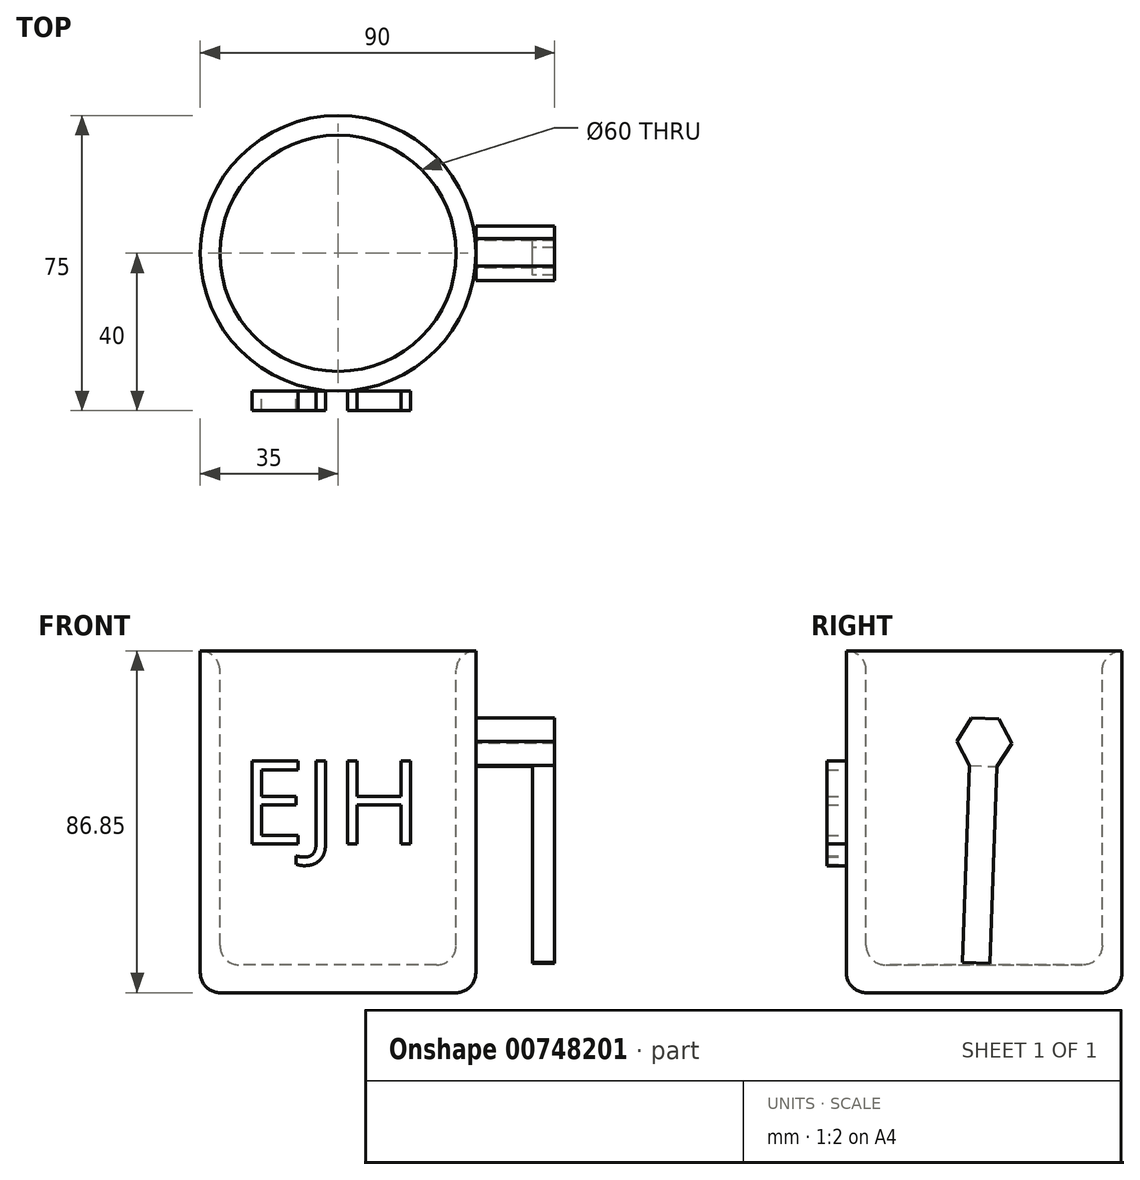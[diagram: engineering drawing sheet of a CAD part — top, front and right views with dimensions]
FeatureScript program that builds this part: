
annotation { "Feature Type Name" : "Feature", "Feature Type Description" : "" }
export const myFeature = defineFeature(function(context is Context, id is Id, definition is map)
    precondition{}
    {
        {
            var Q0;
            Q0=qCreatedBy(makeId("Front.planeOp"),FACE);
            var sketch = newSketch(context, id + "F0", { "sketchPlane" : qUnion([Q0])});
            skLineSegment(sketch, "E0.bottom", {"start": v(35, 49.05) * mm, "end": v(35, 49.05) * mm});
            skLineSegment(sketch, "E0.top", {"start": v(30, -37.8) * mm, "end": v(30, -37.8) * mm});
            skLineSegment(sketch, "E0.left", {"start": v(30, 44.05) * mm, "end": v(30, -25.78) * mm});
            skLineSegment(sketch, "E0.right", {"start": v(35, 32.2) * mm, "end": v(35, -32.8) * mm});
            skLineSegment(sketch, "E1.bottom", {"start": v(30, -37.8) * mm, "end": v(0, -37.8) * mm});
            skLineSegment(sketch, "E1.top", {"start": v(25, -30.78) * mm, "end": v(0, -30.78) * mm});
            skLineSegment(sketch, "E1.left", {"start": v(35, -32.8) * mm, "end": v(35, -30.78) * mm});
            skLineSegment(sketch, "E1.right", {"start": v(0, -37.8) * mm, "end": v(0, -30.78) * mm});
            skLineSegment(sketch, "E2.left", {"start": v(30, 44.05) * mm, "end": v(30, 37.2) * mm});
            skPoint(sketch, "E3.visualSharp", {"position": v(30, -30.78) * mm});
            skArc(sketch, "E3.filletArc", {"start": v(25, -30.78) * mm, "mid": v(28.54, -29.31) * mm, "end": v(30, -25.78) * mm});
            skPoint(sketch, "E4.visualSharp", {"position": v(35, -37.8) * mm});
            skArc(sketch, "E4.filletArc", {"start": v(30, -37.8) * mm, "mid": v(33.54, -36.34) * mm, "end": v(35, -32.8) * mm});
            skPoint(sketch, "E5.visualSharp", {"position": v(30, 49.05) * mm});
            skArc(sketch, "E5.filletArc", {"start": v(35, 49.05) * mm, "mid": v(31.46, 47.58) * mm, "end": v(30, 44.05) * mm});
            skPoint(sketch, "E6.visualSharp", {"position": v(35, 37.2) * mm});
            skLineSegment(sketch, "E7", {"start": v(0, 61.47) * mm, "end": v(0, -66.92) * mm});
            skLineSegment(sketch, "E8", {"start": v(35, 49.05) * mm, "end": v(35, 32.2) * mm});
            skPoint(sketch, "E2.right.end.orphan", {"position": v(44.56, 37.2) * mm});
            skPoint(sketch, "E2.right.start.orphan", {"position": v(44.56, 49.05) * mm});
            skSolve(sketch);
        }
        {
            var Q0;
            Q0=makeQuery(id+"F0.imprint","IMPRINT",FACE,{"disambiguationData":[TD([[makeQuery(id+"F0.imprint","IMPRINT",EDGE,{"derivedFrom":sQuery(id+"F0.wireOp",EDGE,"E0.left")}),1.0]])]});
            var Q1;
            Q1=sQuery(id+"F0.wireOp",EDGE,"E7");
            revolve(context, id + "F1", {"surfaceOperationType" : NewSurfaceOperationType.NEW, "entities" : qUnion([Q0]), "axis" : qUnion([Q1]), "revolveType" : RevolveType.FULL});
        }
        {
            var Q0;
            Q0=qCreatedBy(makeId("Right.planeOp"),FACE);
            cPlane(context, id + "F2", {"entities" : qUnion([Q0]), "cplaneType" : CPlaneType.OFFSET, "offset" : 35 * mm, "width" : 150 * mm, "height" : 150 * mm});
        }
        {
            var Q0;
            Q0=qCreatedBy(id+"F2.planeOp",FACE);
            var sketch = newSketch(context, id + "F3", { "sketchPlane" : qUnion([Q0])});
            skCircle(sketch, "E9.cCircle", {"center": v(0, 25.82) * mm, "radius": 6.05 * mm, "construction": true});
            skLineSegment(sketch, "E9.0", {"start": v(6.98, 25.56) * mm, "end": v(3.27, 19.65) * mm});
            skLineSegment(sketch, "E9.1", {"start": v(3.27, 19.65) * mm, "end": v(-3.72, 19.9) * mm});
            skLineSegment(sketch, "E9.2", {"start": v(-3.72, 19.9) * mm, "end": v(-6.98, 26.08) * mm});
            skLineSegment(sketch, "E9.3", {"start": v(-6.98, 26.08) * mm, "end": v(-3.27, 32) * mm});
            skLineSegment(sketch, "E9.4", {"start": v(-3.27, 32) * mm, "end": v(3.72, 31.74) * mm});
            skLineSegment(sketch, "E9.5", {"start": v(3.72, 31.74) * mm, "end": v(6.98, 25.56) * mm});
            skPoint(sketch, "E9.0.midPoint", {"position": v(5.12, 22.6) * mm});
            skSolve(sketch);
        }
        {
            var Q0;
            Q0=makeQuery(id+"F3.imprint","IMPRINT",FACE,{"disambiguationData":[TD([[makeQuery(id+"F3.imprint","IMPRINT",EDGE,{"derivedFrom":sQuery(id+"F3.wireOp",EDGE,"E9.0")}),-1.0]])]});
            extrude(context, id + "F4", {"entities" : qUnion([Q0]), "depth" : 20 * mm, "offsetDistance" : 25 * mm});
        }
        {
            var Q0;
            Q0=makeQuery(id+"F4.opExtrude","SWEPT_FACE",FACE,{"disambiguationData":[OSD([sQuery(id+"F3.wireOp",EDGE,"E9.1")])]});
            var sketch = newSketch(context, id + "F5", { "sketchPlane" : qUnion([Q0])});
            skLineSegment(sketch, "E10.bottom", {"start": v(49.44, 4.45) * mm, "end": v(55, 4.45) * mm});
            skLineSegment(sketch, "E10.top", {"start": v(49.44, -2.54) * mm, "end": v(55, -2.54) * mm});
            skLineSegment(sketch, "E10.left", {"start": v(49.44, 4.45) * mm, "end": v(49.44, -2.54) * mm});
            skLineSegment(sketch, "E10.right", {"start": v(55, 4.45) * mm, "end": v(55, -2.54) * mm});
            skSolve(sketch);
        }
        {
            var Q0;
            Q0=makeQuery(id+"F5.imprint","IMPRINT",FACE,{"disambiguationData":[TD([[makeQuery(id+"F5.imprint","IMPRINT",EDGE,{"derivedFrom":sQuery(id+"F5.wireOp",EDGE,"E10.bottom")}),1.0]])]});
            extrude(context, id + "F6", {"entities" : qUnion([Q0]), "operationType" : NewBodyOperationType.ADD, "depth" : 50 * mm, "offsetDistance" : 25 * mm});
        }
        {
            var Q0;
            Q0=qCreatedBy(makeId("Front.planeOp"),FACE);
            cPlane(context, id + "F7", {"entities" : qUnion([Q0]), "cplaneType" : CPlaneType.OFFSET, "offset" : 35 * mm, "width" : 150 * mm, "height" : 150 * mm});
        }
        {
            var Q0;
            Q0=qCreatedBy(id+"F7.planeOp",FACE);
            var sketch = newSketch(context, id + "F8", { "sketchPlane" : qUnion([Q0])});
            skText(sketch, "E11", { "text": "EJH", "fontName": "OpenSans-Regular.ttf"});
            const initialGuessF8  = {"E11": [-0.0247, 0, 1, 0, 0.0212]};
            skSetInitialGuess(sketch, initialGuessF8);
            skSolve(sketch);
        }
        {
            var Q0;
            Q0 = qSketchRegion(id + "F8", true);
            extrude(context, id + "F9", {"entities" : qUnion([Q0]), "depth" : 5 * mm, "offsetDistance" : 25 * mm});
        }
    });
